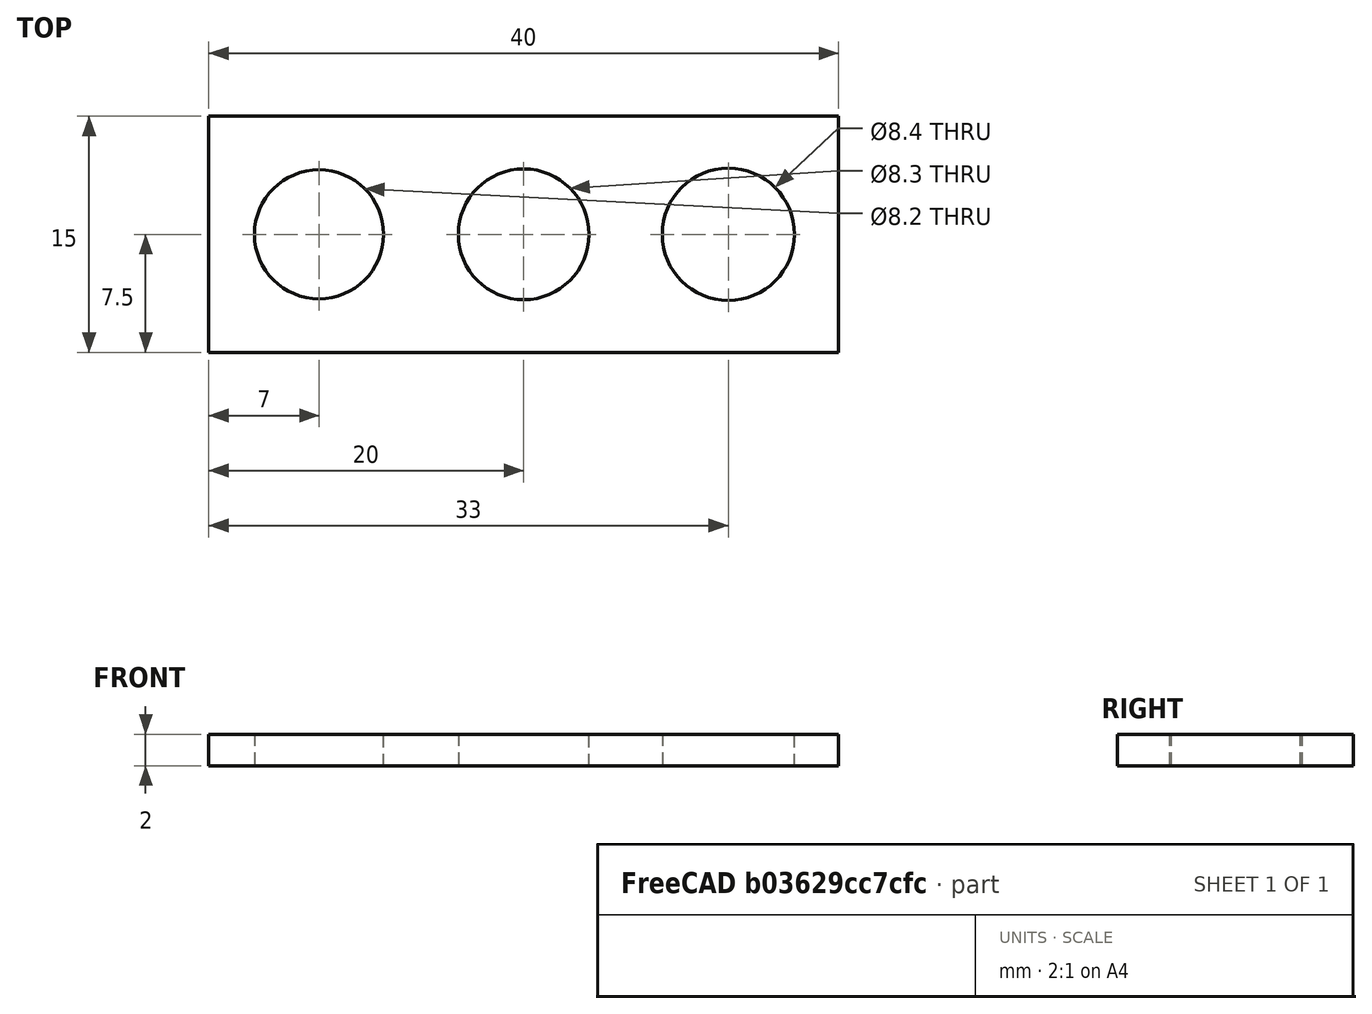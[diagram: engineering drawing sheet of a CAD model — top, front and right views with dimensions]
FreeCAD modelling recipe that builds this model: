
FCSTD DOCUMENT  (FreeCAD 0.18R14555 (Git shallow))
Label: hole-size
License: All rights reserved
LicenseURL: http://en.wikipedia.org/wiki/All_rights_reserved
objects: Sketcher::SketchObject×1, PartDesign::Pad×1, PartDesign::Body×1
note: 4 computed .brp shape members not serialized (recipe doc carries the construction recipe); baked Part::Feature solids carry a one-line shape summary decoded from their .brp

FEATURE [Sketcher::SketchObject] Sketch
  MapMode = 5
  Support = -> [XY_Plane]
  sketch-geometry (12):
    g0: LineSegment StartX=0 StartY=15 StartZ=0 EndX=40 EndY=15 EndZ=0
    g1: LineSegment StartX=40 StartY=15 StartZ=0 EndX=40 EndY=0 EndZ=0
    g2: LineSegment StartX=40 StartY=0 StartZ=0 EndX=0 EndY=0 EndZ=0
    g3: LineSegment StartX=0 StartY=0 StartZ=0 EndX=0 EndY=15 EndZ=0
    g4: Circle CenterX=7 CenterY=7.5 CenterZ=0 NormalX=0 NormalY=0 NormalZ=1 AngleXU=0 Radius=4.1
    g5: Circle CenterX=20 CenterY=7.5 CenterZ=0 NormalX=0 NormalY=0 NormalZ=1 AngleXU=0 Radius=4.15
    g6: Circle CenterX=33 CenterY=7.5 CenterZ=0 NormalX=0 NormalY=0 NormalZ=1 AngleXU=0 Radius=4.2
    g7: LineSegment [constr] StartX=7 StartY=7.5 StartZ=0 EndX=20 EndY=7.5 EndZ=0
    g8: LineSegment [constr] StartX=20 StartY=7.5 StartZ=0 EndX=33 EndY=7.5 EndZ=0
    g9: LineSegment [constr] StartX=7 StartY=7.5 StartZ=0 EndX=0 EndY=15 EndZ=0
    g10: LineSegment [constr] StartX=7 StartY=7.5 StartZ=0 EndX=0 EndY=9e-16 EndZ=0
    g11: LineSegment [constr] StartX=33 StartY=7.5 StartZ=0 EndX=40 EndY=15 EndZ=0
  constraints (30):
    c: Coincident(g0,g1)
    c: Coincident(g1,g2)
    c: Coincident(g2,g3)
    c: Coincident(g3,g0)
    c: Horizontal(g0)
    c: Horizontal(g2)
    c: Vertical(g1)
    c: Vertical(g3)
    c: Coincident(g7,g4)
    c: Coincident(g7,g5)
    c: Horizontal(g7)
    c: Coincident(g8,g5)
    c: Coincident(g8,g6)
    c: Horizontal(g8)
    c: Radius(g4) = 4.1
    c: Radius(g5) = 4.15
    c: Radius(g6) = 4.2
    c: Coincident(g9,g4)
    c: Coincident(g9,g0)
    c: Coincident(g10,g4)
    c: Coincident(g10,g2)
    c: Coincident(g11,g6)
    c: Coincident(g11,g0)
    c: Equal(g8,g7)
    c: Equal(g10,g9)
    c: Equal(g9,g11)
    c: DistanceX(g7,g7) = 13
    c: DistanceX(g2,g2) = 40
    c: DistanceY(g1,g1) = 15
    c: Coincident(g2,g-1)
FEATURE [PartDesign::Pad] Pad
  Length = 2
  Length2 = 100
  Profile = -> Sketch
  Type = 0
FEATURE [PartDesign::Body] Body
  Group = -> [Sketch,Pad]
  Origin = -> Origin
  Tip = -> Pad
